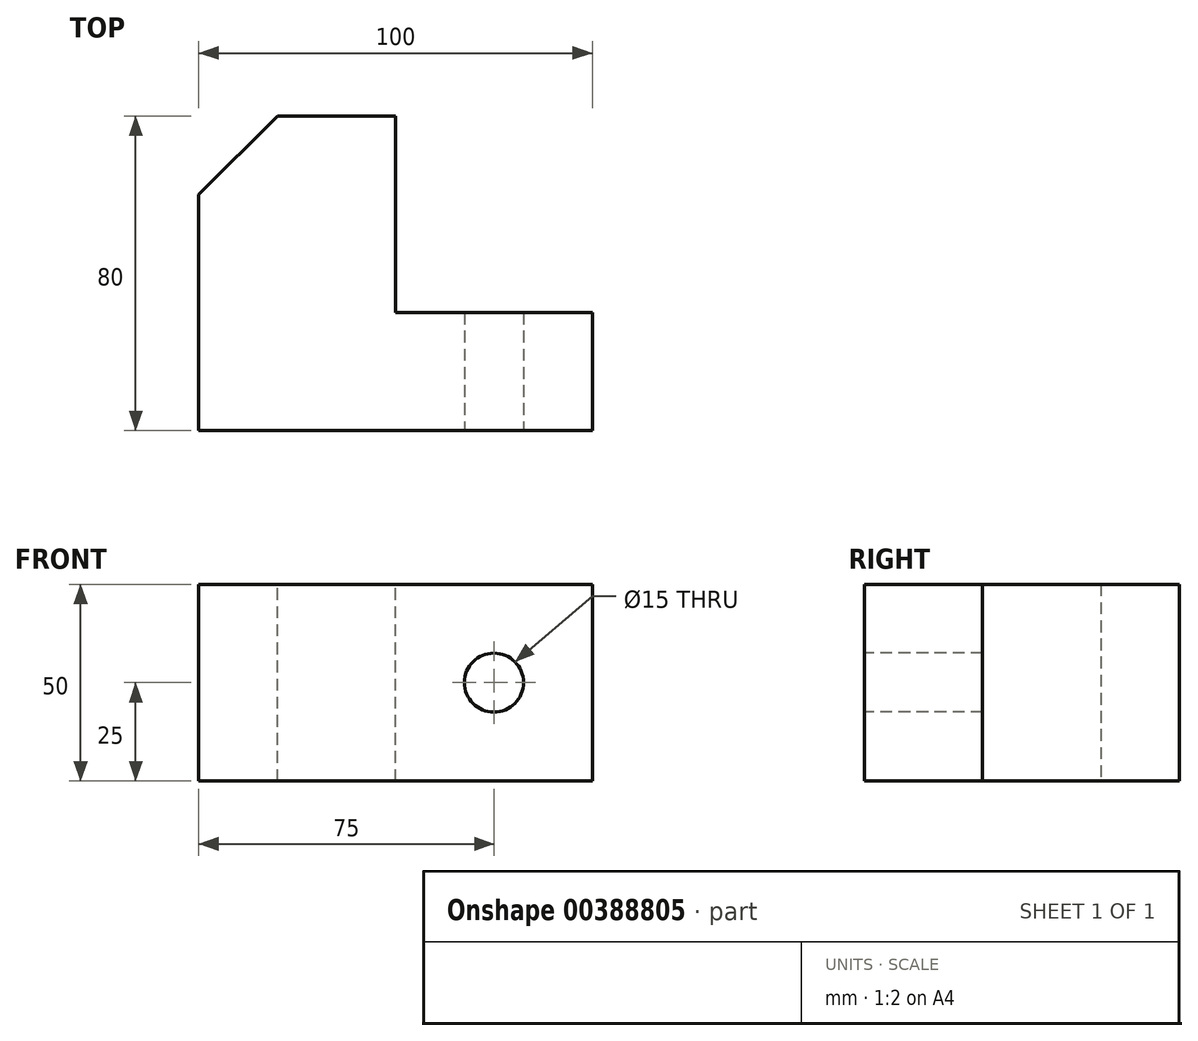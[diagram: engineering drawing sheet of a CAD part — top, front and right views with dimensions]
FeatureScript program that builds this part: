
annotation { "Feature Type Name" : "Feature", "Feature Type Description" : "" }
export const myFeature = defineFeature(function(context is Context, id is Id, definition is map)
    precondition{}
    {
        {
            var Q0;
            Q0=qCreatedBy(makeId("Top.planeOp"),FACE);
            var sketch = newSketch(context, id + "F0", { "sketchPlane" : qUnion([Q0])});
            skLineSegment(sketch, "E0.bottom", {"start": v(0, 0) * mm, "end": v(100, 0) * mm});
            skLineSegment(sketch, "E0.top", {"start": v(0, 80) * mm, "end": v(100, 80) * mm});
            skLineSegment(sketch, "E0.left", {"start": v(0, 0) * mm, "end": v(0, 80) * mm});
            skLineSegment(sketch, "E0.right", {"start": v(100, 0) * mm, "end": v(100, 80) * mm});
            skSolve(sketch);
        }
        {
            var Q0;
            Q0 = qSketchRegion(id + "F0", true);
            extrude(context, id + "F1", {"entities" : qUnion([Q0]), "depth" : 50 * mm});
        }
        {
            var Q0;
            Q0=makeQuery(id+"F1.opExtrude","CAP_FACE",FACE,{"disambiguationData":[OSD([sQuery(id+"F0.wireOp",EDGE,"E0.bottom"),sQuery(id+"F0.wireOp",EDGE,"E0.top"),sQuery(id+"F0.wireOp",EDGE,"E0.left"),sQuery(id+"F0.wireOp",EDGE,"E0.right")])],"isStart":false});
            var sketch = newSketch(context, id + "F2", { "sketchPlane" : qUnion([Q0])});
            skLineSegment(sketch, "E1.bottom", {"start": v(100, 80) * mm, "end": v(50, 80) * mm});
            skLineSegment(sketch, "E1.top", {"start": v(100, 30) * mm, "end": v(50, 30) * mm});
            skLineSegment(sketch, "E1.left", {"start": v(100, 80) * mm, "end": v(100, 30) * mm});
            skLineSegment(sketch, "E1.right", {"start": v(50, 80) * mm, "end": v(50, 30) * mm});
            skSolve(sketch);
        }
        {
            var Q0;
            Q0 = qSketchRegion(id + "F2", true);
            extrude(context, id + "F3", {"entities" : qUnion([Q0]), "operationType" : NewBodyOperationType.REMOVE, "endBound" : BoundingType.UP_TO_NEXT, "oppositeDirection" : true, "depth" : 50 * mm});
        }
        {
            var Q0;
            Q0=makeQuery(id+"F1.opExtrude","SWEPT_EDGE",EDGE,{"disambiguationData":[OSD([sQuery(id+"F0.wireOp",EDGE,"E0.top"),sQuery(id+"F0.wireOp",EDGE,"E0.left")])]});
            chamfer(context, id + "F4", {"entities" : qUnion([Q0]), "width" : 20 * mm, "tangentPropagation" : true});
        }
        {
            var Q0;
            Q0=makeQuery(id+"F1.opExtrude","SWEPT_FACE",FACE,{"disambiguationData":[OSD([sQuery(id+"F0.wireOp",EDGE,"E0.bottom")])]});
            var sketch = newSketch(context, id + "F5", { "sketchPlane" : qUnion([Q0])});
            skLineSegment(sketch, "E2", {"start": v(0, 50) * mm, "end": v(100, 50) * mm});
            skLineSegment(sketch, "E3", {"start": v(100, 50) * mm, "end": v(100, 25) * mm});
            skSolve(sketch);
        }
        {
            var Q0;
            Q0=makeQuery(id+"F5.imprint","IMPRINT",FACE,{"disambiguationData":[TD([[makeQuery(id+"F5.imprint","IMPRINT",EDGE,{"derivedFrom":sQuery(id+"F5.wireOp",EDGE,"E2")}),-1.0]])]});
            var sketch = newSketch(context, id + "F6", { "sketchPlane" : qUnion([Q0])});
            skLineSegment(sketch, "E4", {"start": v(0, 0) * mm, "end": v(75, 0) * mm});
            skLineSegment(sketch, "E5", {"start": v(75, 0) * mm, "end": v(75, 25) * mm});
            skCircle(sketch, "E6", {"center": v(75, 25) * mm, "radius": 7.5 * mm});
            skSolve(sketch);
        }
        {
            var Q0;
            Q0=makeQuery(id+"F6.imprint","IMPRINT",FACE,{"disambiguationData":[TD([[makeQuery(id+"F6.imprint","IMPRINT",EDGE,{"derivedFrom":sQuery(id+"F6.wireOp",EDGE,"E6")}),1.0]])]});
            extrude(context, id + "F7", {"entities" : qUnion([Q0]), "operationType" : NewBodyOperationType.REMOVE, "endBound" : BoundingType.THROUGH_ALL, "oppositeDirection" : true, "depth" : 25 * mm});
        }
    });
